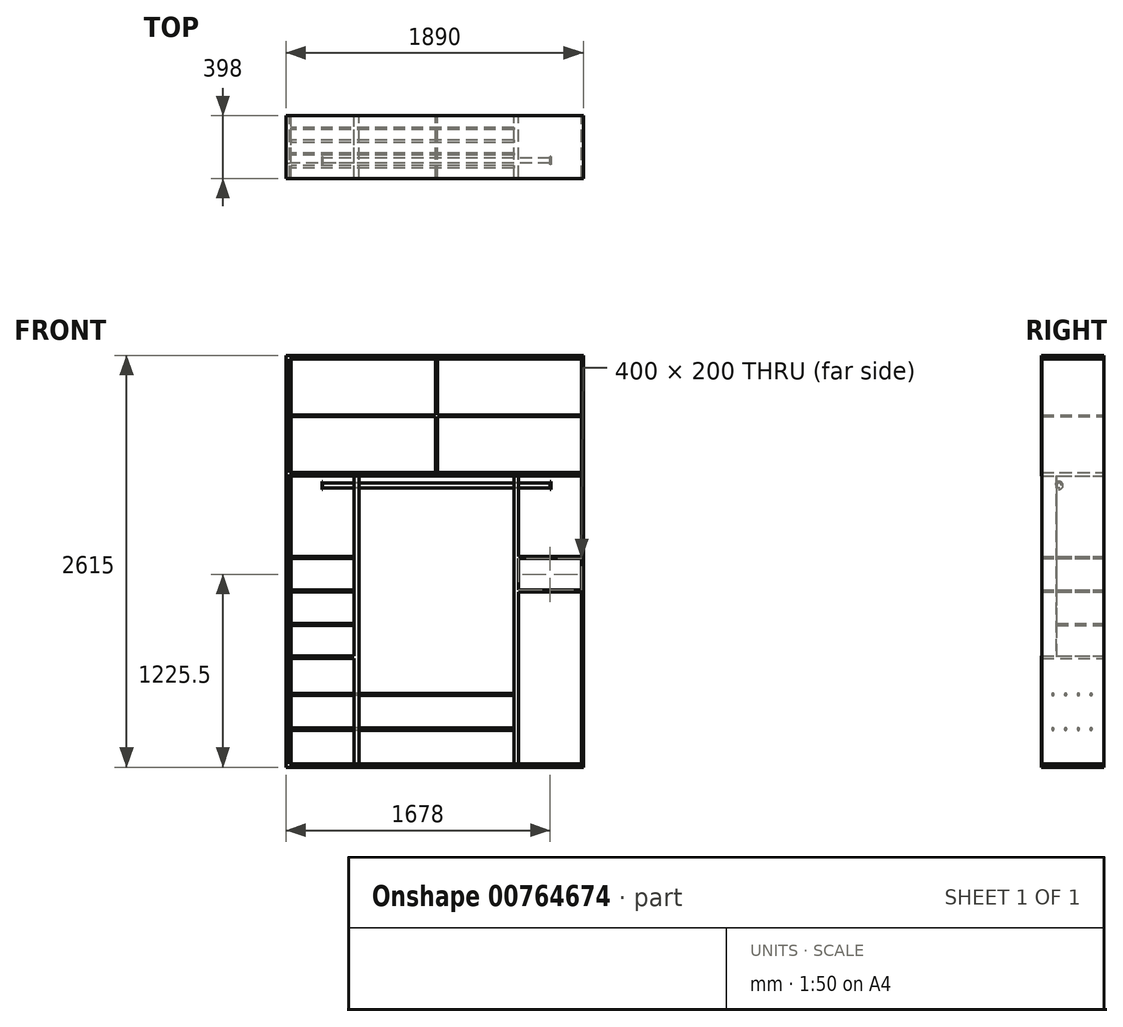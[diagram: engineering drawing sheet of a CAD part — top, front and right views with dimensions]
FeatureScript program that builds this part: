
annotation { "Feature Type Name" : "Feature", "Feature Type Description" : "" }
export const myFeature = defineFeature(function(context is Context, id is Id, definition is map)
    precondition{}
    {
        {
            var Q0;
            Q0=qCreatedBy(makeId("Front.planeOp"),FACE);
            var sketch = newSketch(context, id + "F0", { "sketchPlane" : qUnion([Q0])});
            skLineSegment(sketch, "E0.bottom", {"start": v(0, 0) * mm, "end": v(-1890, 0) * mm});
            skLineSegment(sketch, "E0.top", {"start": v(0, 2615) * mm, "end": v(-1890, 2615) * mm});
            skLineSegment(sketch, "E0.left", {"start": v(0, 0) * mm, "end": v(0, 2615) * mm});
            skLineSegment(sketch, "E0.right", {"start": v(-1890, 0) * mm, "end": v(-1890, 2615) * mm});
            skLineSegment(sketch, "E1", {"start": v(-1868, 2593) * mm, "end": v(0, 2593) * mm});
            skLineSegment(sketch, "E2", {"start": v(-1868, 2593) * mm, "end": v(-1868, 1872) * mm});
            skLineSegment(sketch, "E3", {"start": v(-1868, 22) * mm, "end": v(0, 22) * mm});
            skLineSegment(sketch, "E4", {"start": v(-1868, 1872) * mm, "end": v(-12, 1872) * mm});
            skLineSegment(sketch, "E5", {"start": v(-1868, 1850) * mm, "end": v(-12, 1850) * mm});
            skLineSegment(sketch, "E6", {"start": v(-1456, 1850) * mm, "end": v(-1456, 22) * mm});
            skLineSegment(sketch, "E7", {"start": v(-1426, 1850) * mm, "end": v(-1426, 22) * mm});
            skLineSegment(sketch, "E8", {"start": v(-412, 1850) * mm, "end": v(-412, 22) * mm});
            skLineSegment(sketch, "E9", {"start": v(-442, 1850) * mm, "end": v(-442, 22) * mm});
            skLineSegment(sketch, "E10", {"start": v(-1856, 2593) * mm, "end": v(-1856, 2238.5) * mm});
            skLineSegment(sketch, "E11", {"start": v(-12, 2593) * mm, "end": v(-12, 2238.5) * mm});
            skLineSegment(sketch, "E12.trimOffspring", {"start": v(-1856, 1850) * mm, "end": v(-1856, 22) * mm});
            skLineSegment(sketch, "E13.trimOffspring", {"start": v(-1868, 1850) * mm, "end": v(-1868, 22) * mm});
            skLineSegment(sketch, "E14", {"start": v(-940, 2593) * mm, "end": v(-940, 2238.5) * mm});
            skLineSegment(sketch, "E15", {"start": v(-928, 2593) * mm, "end": v(-928, 2238.5) * mm});
            skPoint(sketch, "E16", {"position": v(-934, 1872) * mm});
            skLineSegment(sketch, "E17", {"start": v(-1856, 2238.5) * mm, "end": v(-940, 2238.5) * mm});
            skLineSegment(sketch, "E18", {"start": v(-1856, 2226.5) * mm, "end": v(-940, 2226.5) * mm});
            skLineSegment(sketch, "E19.trimOffspring", {"start": v(-1856, 2226.5) * mm, "end": v(-1856, 1872) * mm});
            skLineSegment(sketch, "E20.trimOffspring", {"start": v(-928, 2226.5) * mm, "end": v(-928, 1872) * mm});
            skLineSegment(sketch, "E21.trimOffspring", {"start": v(-940, 2226.5) * mm, "end": v(-940, 1872) * mm});
            skLineSegment(sketch, "E22.trimOffspring", {"start": v(-928, 2238.5) * mm, "end": v(-12, 2238.5) * mm});
            skLineSegment(sketch, "E23.trimOffspring", {"start": v(-928, 2226.5) * mm, "end": v(-12, 2226.5) * mm});
            skLineSegment(sketch, "E24.trimOffspring", {"start": v(-12, 2226.5) * mm, "end": v(-12, 22) * mm});
            skSolve(sketch);
        }
        {
            var Q0;
            {var subQ25=sQuery(id+"F0.wireOp",EDGE,"E0.bottom");Q0=makeQuery(id+"F0.imprint","IMPRINT",FACE,{"disambiguationData":[TD([[makeQuery(id+"F0.imprint","IMPRINT",EDGE,{"derivedFrom":subQ25}),-1.0]])]});}
            extrude(context, id + "F1", {"entities" : qUnion([Q0]), "depth" : 398 * mm, "offsetDistance" : 25 * mm});
        }
        {
            var Q0;
            {var subQ0=sQuery(id+"F0.wireOp",EDGE,"E6");Q0=makeQuery(id+"F0.imprint","IMPRINT",FACE,{"disambiguationData":[TD([[makeQuery(id+"F0.imprint","IMPRINT",EDGE,{"derivedFrom":subQ0}),1.0]])]});}
            var Q1;
            {var subQ0=sQuery(id+"F0.wireOp",EDGE,"E8");Q1=makeQuery(id+"F0.imprint","IMPRINT",FACE,{"disambiguationData":[TD([[makeQuery(id+"F0.imprint","IMPRINT",EDGE,{"derivedFrom":subQ0}),-1.0]])]});}
            var Q2;
            {var subQ1=sQuery(id+"F0.wireOp",EDGE,"E2");Q2=makeQuery(id+"F0.imprint","IMPRINT",FACE,{"disambiguationData":[TD([[makeQuery(id+"F0.imprint","IMPRINT",EDGE,{"derivedFrom":subQ1}),1.0]])]});}
            var Q3;
            {var subQ2=sQuery(id+"F0.wireOp",EDGE,"E12.trimOffspring");Q3=makeQuery(id+"F0.imprint","IMPRINT",FACE,{"disambiguationData":[TD([[makeQuery(id+"F0.imprint","IMPRINT",EDGE,{"derivedFrom":subQ2}),-1.0]])]});}
            var Q4;
            Q4=makeQuery(id+"F1.opExtrude","CAP_FACE",FACE,{"disambiguationData":[OSD([sQuery(id+"F0.wireOp",EDGE,"E0.bottom"),sQuery(id+"F0.wireOp",EDGE,"E0.top"),sQuery(id+"F0.wireOp",EDGE,"E0.left"),sQuery(id+"F0.wireOp",EDGE,"E0.right"),sQuery(id+"F0.wireOp",EDGE,"E1"),sQuery(id+"F0.wireOp",EDGE,"E2"),sQuery(id+"F0.wireOp",EDGE,"E3"),sQuery(id+"F0.wireOp",EDGE,"E4"),sQuery(id+"F0.wireOp",EDGE,"E5"),sQuery(id+"F0.wireOp",EDGE,"E13.trimOffspring"),sQuery(id+"F0.wireOp",EDGE,"E24.trimOffspring")])],"isStart":false});
            extrude(context, id + "F2", {"entities" : qUnion([Q0, Q1, Q2, Q3]), "endBound" : BoundingType.UP_TO_SURFACE, "depth" : 25 * mm, "endBoundEntityFace" : qUnion([Q4]), "hasOffset" : true, "offsetDistance" : 5 * mm});
        }
        {
            var Q0;
            Q0=makeQuery(id+"F2.opExtrude","SWEPT_FACE",FACE,{"disambiguationData":[OSD([sQuery(id+"F0.wireOp",EDGE,"E12.trimOffspring")])]});
            var sketch = newSketch(context, id + "F3", { "sketchPlane" : qUnion([Q0])});
            skCircle(sketch, "E25", {"center": v(-324.5, 242) * mm, "radius": 7.5 * mm});
            skCircle(sketch, "E26.0.1.0", {"center": v(-324.5, 462) * mm, "radius": 7.5 * mm});
            skCircle(sketch, "E26.1.0.0", {"center": v(-243.5, 242) * mm, "radius": 7.5 * mm});
            skCircle(sketch, "E26.1.1.0", {"center": v(-243.5, 462) * mm, "radius": 7.5 * mm});
            skCircle(sketch, "E26.2.0.0", {"center": v(-162.5, 242) * mm, "radius": 7.5 * mm});
            skCircle(sketch, "E26.2.1.0", {"center": v(-162.5, 462) * mm, "radius": 7.5 * mm});
            skCircle(sketch, "E26.3.0.0", {"center": v(-81.5, 242) * mm, "radius": 7.5 * mm});
            skCircle(sketch, "E26.3.1.0", {"center": v(-81.5, 462) * mm, "radius": 7.5 * mm});
            skLineSegment(sketch, "E26.direction1", {"start": v(-324.5, 242) * mm, "end": v(-243.5, 242) * mm, "construction": true});
            skLineSegment(sketch, "E26.direction2", {"start": v(-324.5, 242) * mm, "end": v(-324.5, 462) * mm, "construction": true});
            skSolve(sketch);
        }
        {
            var Q0;
            Q0 = qSketchRegion(id + "F3", true);
            var Q1;
            Q1=makeQuery(id+"F2.opExtrude","SWEPT_FACE",FACE,{"disambiguationData":[OSD([sQuery(id+"F0.wireOp",EDGE,"E9")])]});
            extrude(context, id + "F4", {"entities" : qUnion([Q0]), "endBound" : BoundingType.UP_TO_SURFACE, "depth" : 25 * mm, "endBoundEntityFace" : qUnion([Q1]), "offsetDistance" : 25 * mm});
        }
        {
            var Q0;
            Q0=qCreatedBy(makeId("Front.planeOp"),FACE);
            var sketch = newSketch(context, id + "F5", { "sketchPlane" : qUnion([Q0])});
            skLineSegment(sketch, "E27.bottom", {"start": v(-1856, 701.5) * mm, "end": v(-1456, 701.5) * mm});
            skLineSegment(sketch, "E27.top", {"start": v(-1856, 689.5) * mm, "end": v(-1456, 689.5) * mm});
            skLineSegment(sketch, "E27.left", {"start": v(-1856, 701.5) * mm, "end": v(-1856, 689.5) * mm});
            skLineSegment(sketch, "E27.right", {"start": v(-1456, 701.5) * mm, "end": v(-1456, 689.5) * mm});
            skLineSegment(sketch, "E28", {"start": v(-1856, 469.5) * mm, "end": v(-442, 469.5) * mm, "construction": true});
            skLineSegment(sketch, "E29.0.1.0", {"start": v(-1856, 913.5) * mm, "end": v(-1456, 913.5) * mm});
            skLineSegment(sketch, "E29.0.1.1", {"start": v(-1856, 901.5) * mm, "end": v(-1456, 901.5) * mm});
            skLineSegment(sketch, "E29.0.1.2", {"start": v(-1856, 913.5) * mm, "end": v(-1856, 901.5) * mm});
            skLineSegment(sketch, "E29.0.1.3", {"start": v(-1456, 913.5) * mm, "end": v(-1456, 901.5) * mm});
            skLineSegment(sketch, "E29.0.2.0", {"start": v(-1856, 1125.5) * mm, "end": v(-1456, 1125.5) * mm});
            skLineSegment(sketch, "E29.0.2.1", {"start": v(-1856, 1113.5) * mm, "end": v(-1456, 1113.5) * mm});
            skLineSegment(sketch, "E29.0.2.2", {"start": v(-1856, 1125.5) * mm, "end": v(-1856, 1113.5) * mm});
            skLineSegment(sketch, "E29.0.2.3", {"start": v(-1456, 1125.5) * mm, "end": v(-1456, 1113.5) * mm});
            skLineSegment(sketch, "E29.0.3.0", {"start": v(-1856, 1337.5) * mm, "end": v(-1456, 1337.5) * mm});
            skLineSegment(sketch, "E29.0.3.1", {"start": v(-1856, 1325.5) * mm, "end": v(-1456, 1325.5) * mm});
            skLineSegment(sketch, "E29.0.3.2", {"start": v(-1856, 1337.5) * mm, "end": v(-1856, 1325.5) * mm});
            skLineSegment(sketch, "E29.0.3.3", {"start": v(-1456, 1337.5) * mm, "end": v(-1456, 1325.5) * mm});
            skLineSegment(sketch, "E29.direction1", {"start": v(-1856, 701.5) * mm, "end": v(-1831, 701.5) * mm, "construction": true});
            skLineSegment(sketch, "E29.direction2", {"start": v(-1856, 701.5) * mm, "end": v(-1856, 913.5) * mm, "construction": true});
            skLineSegment(sketch, "E30.bottom", {"start": v(-412, 1337.5) * mm, "end": v(-12, 1337.5) * mm});
            skLineSegment(sketch, "E30.top", {"start": v(-412, 1325.5) * mm, "end": v(-12, 1325.5) * mm});
            skLineSegment(sketch, "E30.left", {"start": v(-412, 1337.5) * mm, "end": v(-412, 1325.5) * mm});
            skLineSegment(sketch, "E30.right", {"start": v(-12, 1337.5) * mm, "end": v(-12, 1325.5) * mm});
            skLineSegment(sketch, "E31.bottom", {"start": v(-412, 1125.5) * mm, "end": v(-12, 1125.5) * mm});
            skLineSegment(sketch, "E31.top", {"start": v(-412, 1113.5) * mm, "end": v(-12, 1113.5) * mm});
            skLineSegment(sketch, "E31.left", {"start": v(-412, 1125.5) * mm, "end": v(-412, 1113.5) * mm});
            skLineSegment(sketch, "E31.right", {"start": v(-12, 1125.5) * mm, "end": v(-12, 1113.5) * mm});
            skSolve(sketch);
        }
        {
            var Q0;
            Q0=makeQuery(id+"F5.imprint","IMPRINT",FACE,{"disambiguationData":[TD([[makeQuery(id+"F5.imprint","IMPRINT",EDGE,{"derivedFrom":sQuery(id+"F5.wireOp",EDGE,"E29.0.3.0")}),-1.0]])]});
            var Q1;
            Q1=makeQuery(id+"F5.imprint","IMPRINT",FACE,{"disambiguationData":[TD([[makeQuery(id+"F5.imprint","IMPRINT",EDGE,{"derivedFrom":sQuery(id+"F5.wireOp",EDGE,"E29.0.2.0")}),-1.0]])]});
            var Q2;
            Q2=makeQuery(id+"F5.imprint","IMPRINT",FACE,{"disambiguationData":[TD([[makeQuery(id+"F5.imprint","IMPRINT",EDGE,{"derivedFrom":sQuery(id+"F5.wireOp",EDGE,"E29.0.1.0")}),-1.0]])]});
            var Q3;
            Q3=makeQuery(id+"F5.imprint","IMPRINT",FACE,{"disambiguationData":[TD([[makeQuery(id+"F5.imprint","IMPRINT",EDGE,{"derivedFrom":sQuery(id+"F5.wireOp",EDGE,"E27.bottom")}),-1.0]])]});
            var Q4;
            Q4=makeQuery(id+"F5.imprint","IMPRINT",FACE,{"disambiguationData":[TD([[makeQuery(id+"F5.imprint","IMPRINT",EDGE,{"derivedFrom":sQuery(id+"F5.wireOp",EDGE,"E30.bottom")}),-1.0]])]});
            var Q5;
            Q5=makeQuery(id+"F5.imprint","IMPRINT",FACE,{"disambiguationData":[TD([[makeQuery(id+"F5.imprint","IMPRINT",EDGE,{"derivedFrom":sQuery(id+"F5.wireOp",EDGE,"E31.bottom")}),-1.0]])]});
            var Q6;
            Q6=makeQuery(id+"F2.opExtrude","CAP_FACE",FACE,{"disambiguationData":[OSD([sQuery(id+"F0.wireOp",EDGE,"E3"),sQuery(id+"F0.wireOp",EDGE,"E5"),sQuery(id+"F0.wireOp",EDGE,"E6"),sQuery(id+"F0.wireOp",EDGE,"E7")])],"isStart":false});
            extrude(context, id + "F6", {"entities" : qUnion([Q0, Q1, Q2, Q3, Q4, Q5]), "operationType" : NewBodyOperationType.ADD, "endBound" : BoundingType.UP_TO_SURFACE, "depth" : 25 * mm, "endBoundEntityFace" : qUnion([Q6]), "offsetDistance" : 25 * mm});
        }
        {
            var Q0;
            Q0=makeQuery(id+"F1.opExtrude","SWEPT_FACE",FACE,{"disambiguationData":[OSD([sQuery(id+"F0.wireOp",EDGE,"E0.right")])]});
            var sketch = newSketch(context, id + "F7", { "sketchPlane" : qUnion([Q0])});
            skLineSegment(sketch, "E32.0", {"start": v(976.94, 1850) * mm, "end": v(300, 1850) * mm});
            skLineSegment(sketch, "E33.0", {"start": v(964.39, 701.5) * mm, "end": v(300, 701.5) * mm});
            skPoint(sketch, "E34.orphan", {"position": v(393, 701.5) * mm});
            skPoint(sketch, "E35.orphan", {"position": v(393, 1850) * mm});
            skLineSegment(sketch, "E36", {"start": v(300, 1850) * mm, "end": v(300, 701.5) * mm});
            skLineSegment(sketch, "E37", {"start": v(976.94, 1850) * mm, "end": v(964.39, 701.5) * mm});
            skSolve(sketch);
        }
        {
            var Q0;
            Q0 = qSketchRegion(id + "F7", true);
            var Q1;
            {var subQ13=sQuery(id+"F0.wireOp",EDGE,"E6");var subQ16=sQuery(id+"F5.wireOp",EDGE,"E29.0.3.0");Q1=makeQuery(id+"F6.boolean.opBoolean","SPLIT",FACE,{"disambiguationData":[TD([makeQuery(id+"F6.opExtrude","SWEPT_FACE",FACE,{"disambiguationData":[OSD([subQ16])]})])],"derivedFrom":makeQuery(id+"F2.opExtrude","SWEPT_FACE",FACE,{"disambiguationData":[OSD([subQ13])]})});}
            extrude(context, id + "F8", {"entities" : qUnion([Q0]), "operationType" : NewBodyOperationType.REMOVE, "endBound" : BoundingType.UP_TO_SURFACE, "oppositeDirection" : true, "depth" : 25 * mm, "endBoundEntityFace" : qUnion([Q1]), "offsetDistance" : 25 * mm});
        }
        {
            var Q0;
            Q0=makeQuery(id+"F8.boolean.opBoolean","COPY",FACE,{"disambiguationData":[TD([makeQuery(id+"F1.opExtrude","SWEPT_FACE",FACE,{"disambiguationData":[OSD([sQuery(id+"F0.wireOp",EDGE,"E0.right")])]})])],"derivedFrom":makeQuery(id+"F8.opExtrude","SWEPT_FACE",FACE,{"disambiguationData":[OSD([sQuery(id+"F7.wireOp",EDGE,"E36")])]})});
            extrude(context, id + "F9", {"entities" : qUnion([Q0]), "operationType" : NewBodyOperationType.ADD, "depth" : 5 * mm, "offsetDistance" : 25 * mm});
        }
        {
            var Q0;
            {var subQ1=sQuery(id+"F0.wireOp",EDGE,"E0.right");Q0=makeQuery(id+"F8.boolean.opBoolean","COPY",FACE,{"disambiguationData":[TD([makeQuery(id+"F1.opExtrude","SWEPT_FACE",FACE,{"disambiguationData":[OSD([subQ1])]})])],"derivedFrom":makeQuery(id+"F8.opExtrude","SWEPT_FACE",FACE,{"disambiguationData":[OSD([sQuery(id+"F7.wireOp",EDGE,"E33.0")])]})});}
            extrude(context, id + "F10", {"entities" : qUnion([Q0]), "operationType" : NewBodyOperationType.ADD, "depth" : 5 * mm, "offsetDistance" : 25 * mm});
        }
        {
            var Q0;
            Q0=makeQuery(id+"F2.opExtrude","SWEPT_FACE",FACE,{"disambiguationData":[OSD([sQuery(id+"F0.wireOp",EDGE,"E7")])]});
            var sketch = newSketch(context, id + "F11", { "sketchPlane" : qUnion([Q0])});
            skCircle(sketch, "E38", {"center": v(-285, 1790) * mm, "radius": 15 * mm});
            skLineSegment(sketch, "E39.0", {"start": v(-393, 22) * mm, "end": v(0, 22) * mm, "construction": true});
            skSolve(sketch);
        }
        {
            var Q0;
            Q0 = qSketchRegion(id + "F11", true);
            var Q1;
            Q1=makeQuery(id+"F2.opExtrude","SWEPT_FACE",FACE,{"disambiguationData":[OSD([sQuery(id+"F0.wireOp",EDGE,"E8")])]});
            var Q2;
            {var subQ3=sQuery(id+"F5.wireOp",EDGE,"E29.0.2.0");var subQ8=sQuery(id+"F5.wireOp",EDGE,"E29.0.3.0");var subQ13=sQuery(id+"F5.wireOp",EDGE,"E29.0.1.0");var subQ17=sQuery(id+"F0.wireOp",EDGE,"E6");var subQ25=sQuery(id+"F5.wireOp",EDGE,"E27.bottom");var subQ30=makeQuery(id+"F2.opExtrude","SWEPT_FACE",FACE,{"disambiguationData":[OSD([subQ17])]});Q2=makeQuery(id+"F8.boolean.opBoolean","MERGE",FACE,{"derivedFrom":[makeQuery(id+"F6.boolean.opBoolean","SPLIT",FACE,{"disambiguationData":[TD([makeQuery(id+"F6.opExtrude","SWEPT_FACE",FACE,{"disambiguationData":[OSD([subQ8])]})])],"derivedFrom":subQ30}),makeQuery(id+"F6.boolean.opBoolean","SPLIT",FACE,{"disambiguationData":[TD([makeQuery(id+"F6.opExtrude","SWEPT_FACE",FACE,{"disambiguationData":[OSD([subQ25])]})])],"derivedFrom":subQ30}),makeQuery(id+"F6.boolean.opBoolean","SPLIT",FACE,{"disambiguationData":[TD([makeQuery(id+"F6.opExtrude","SWEPT_FACE",FACE,{"disambiguationData":[OSD([subQ13])]})])],"derivedFrom":subQ30}),makeQuery(id+"F6.boolean.opBoolean","SPLIT",FACE,{"disambiguationData":[TD([makeQuery(id+"F6.opExtrude","SWEPT_FACE",FACE,{"disambiguationData":[OSD([subQ3])]})])],"derivedFrom":subQ30})],"fromTools":[makeQuery(id+"F8.opExtrude","CAP_FACE",FACE,{"disambiguationData":[OSD([sQuery(id+"F7.wireOp",EDGE,"E32.0"),sQuery(id+"F7.wireOp",EDGE,"E33.0"),sQuery(id+"F7.wireOp",EDGE,"E36"),sQuery(id+"F7.wireOp",EDGE,"E37")])],"isStart":false})]});}
            extrude(context, id + "F12", {"entities" : qUnion([Q0]), "endBound" : BoundingType.UP_TO_SURFACE, "depth" : 25 * mm, "endBoundEntityFace" : qUnion([Q1]), "hasOffset" : true, "offsetDistance" : 200 * mm, "offsetOppositeDirection" : true, "hasSecondDirection" : true, "secondDirectionBound" : BoundingType.UP_TO_SURFACE, "secondDirectionOppositeDirection" : true, "secondDirectionDepth" : 25 * mm, "secondDirectionBoundEntityFace" : qUnion([Q2]), "hasSecondDirectionOffset" : true, "secondDirectionOffsetDistance" : 200 * mm, "secondDirectionOffsetOppositeDirection" : true});
        }
        {
            var Q0;
            Q0=makeQuery(id+"F12.opExtrude","CAP_FACE",FACE,{"disambiguationData":[OSD([sQuery(id+"F11.wireOp",EDGE,"E38")])],"isStart":true});
            var sketch = newSketch(context, id + "F13", { "sketchPlane" : qUnion([Q0])});
            skCircle(sketch, "E40.0", {"center": v(285, 1790) * mm, "radius": 25 * mm});
            skSolve(sketch);
        }
        {
            var Q0;
            Q0=makeQuery(id+"F13.imprint","IMPRINT",FACE,{"disambiguationData":[TD([[makeQuery(id+"F13.imprint","IMPRINT",EDGE,{"derivedFrom":makeQuery(id+"F12.opExtrude","CAP_EDGE",EDGE,{"disambiguationData":[OSD([sQuery(id+"F11.wireOp",EDGE,"E38")])],"isStart":true})}),-1.0]])]});
            var Q1;
            Q1=makeQuery(id+"F13.imprint","IMPRINT",FACE,{"disambiguationData":[TD([[makeQuery(id+"F13.imprint","IMPRINT",EDGE,{"derivedFrom":sQuery(id+"F13.wireOp",EDGE,"E40.0")}),1.0]])]});
            var Q2;
            Q2=sQuery(id+"F13.wireOp",EDGE,"E40.0");
            extrude(context, id + "F14", {"entities" : qUnion([Q0, Q1]), "surfaceEntities" : qUnion([Q2]), "depth" : 5 * mm, "offsetDistance" : 25 * mm});
        }
        {
            var Q0;
            Q0=makeQuery(id+"F12.opExtrude","CAP_FACE",FACE,{"disambiguationData":[OSD([sQuery(id+"F11.wireOp",EDGE,"E38")])],"isStart":false});
            var sketch = newSketch(context, id + "F15", { "sketchPlane" : qUnion([Q0])});
            skCircle(sketch, "E41.0", {"center": v(-285, 1790) * mm, "radius": 25 * mm});
            skSolve(sketch);
        }
        {
            var Q0;
            Q0=makeQuery(id+"F15.imprint","IMPRINT",FACE,{"disambiguationData":[TD([[makeQuery(id+"F15.imprint","IMPRINT",EDGE,{"derivedFrom":makeQuery(id+"F12.opExtrude","CAP_EDGE",EDGE,{"disambiguationData":[OSD([sQuery(id+"F11.wireOp",EDGE,"E38")])],"isStart":false})}),1.0]])]});
            var Q1;
            Q1=makeQuery(id+"F15.imprint","IMPRINT",FACE,{"disambiguationData":[TD([[makeQuery(id+"F15.imprint","IMPRINT",EDGE,{"derivedFrom":sQuery(id+"F15.wireOp",EDGE,"E41.0")}),1.0]])]});
            extrude(context, id + "F16", {"entities" : qUnion([Q0, Q1]), "depth" : 5 * mm, "offsetDistance" : 25 * mm});
        }
    });
